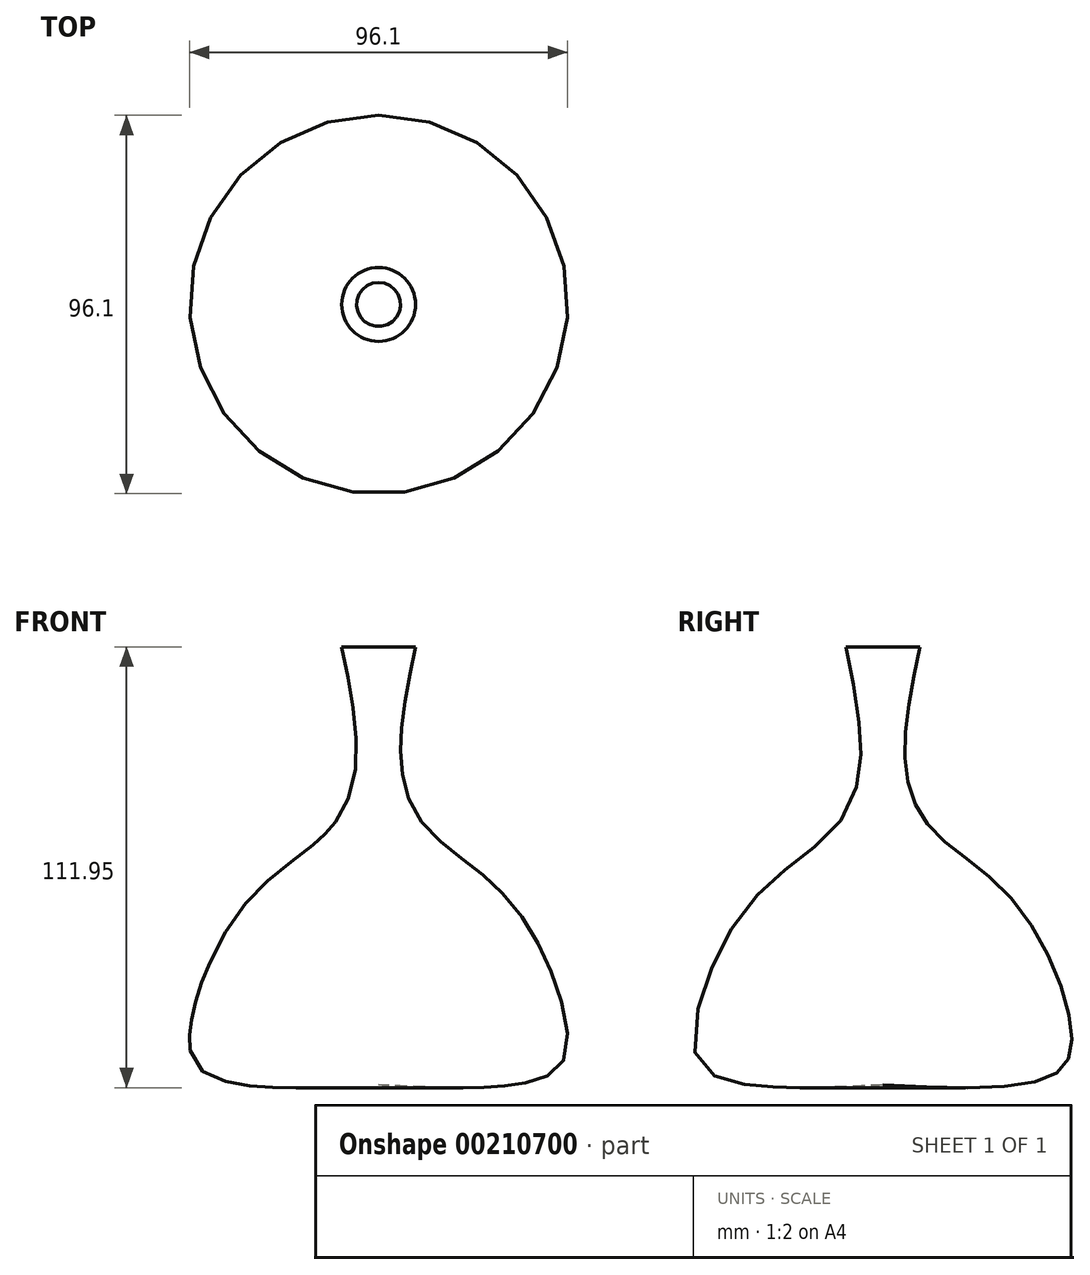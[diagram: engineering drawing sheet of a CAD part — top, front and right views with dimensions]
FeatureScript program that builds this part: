
annotation { "Feature Type Name" : "Feature", "Feature Type Description" : "" }
export const myFeature = defineFeature(function(context is Context, id is Id, definition is map)
    precondition{}
    {
        {
            var Q0;
            Q0=qCreatedBy(makeId("Right.planeOp"),FACE);
            var sketch = newSketch(context, id + "F0", { "sketchPlane" : qUnion([Q0])});
            skFitSpline(sketch, "E0", {"points": [v(9.38, 54.55) * mm, v(5.63, 27.04) * mm, v(11.88, 8.9) * mm, v(33.13, -9.85) * mm, v(47.82, -42.04) * mm, v(43.76, -53.92) * mm, v(0, -56.73) * mm], "startDerivative": vector(-35.38, -169.3) * mm, "endDerivative": vector(-256.3, 11.89) * mm});
            skLineSegment(sketch, "E1", {"start": v(0, 66.74) * mm, "end": v(0, 49.86) * mm});
            skSolve(sketch);
        }
        {
            var Q0;
            Q0=sQuery(id+"F0.wireOp",EDGE,"E0");
            var Q1;
            Q1=sQuery(id+"F0.wireOp",EDGE,"E1");
            revolve(context, id + "F1", {"bodyType" : ToolBodyType.SURFACE, "surfaceEntities" : qUnion([Q0]), "axis" : qUnion([Q1]), "revolveType" : RevolveType.FULL});
        }
    });
